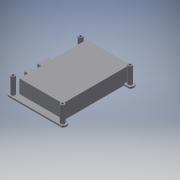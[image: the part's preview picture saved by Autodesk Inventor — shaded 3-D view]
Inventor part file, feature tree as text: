
AUTODESK INVENTOR PART (.ipt)
format: ipt  version: 2019 (Build 230136000, 136)  size: 1,348,608 bytes
history: native  units: mm
features: sketch x7, extrude x5, other x1
ambient origin geometry x8: Origin, YZ Plane, XZ Plane, XY Plane, X Axis, Y Axis, Z Axis, Center Point
bodies: Solid1 (feature_tree)
feature tree (13):
  extrude  "Extrusion1"  Depth=98.58mm
  extrude  "Extrusion2"  Depth=90.0mm
  extrude  "Extrusion3"  Depth=3.0mm
  extrude  "Extrusion4"  Depth=3.0mm
  sketch  "Sketch6"  dims[d8=76.54mm d9=98.58mm]
  extrude  "Extrusion5"  Depth=98.58mm
  sketch  "Sketch8"  dims[d11=81.43mm d12=7.0mm d13=7.0mm d14=2.0mm d15=0.0mm d16=58.04mm d17=98.58mm d18=90.0mm d19=18.0mm d20=0.0mm d21=46.0mm d22=15.0mm d23=20.0mm d24=15.0mm d25=20.0mm d26=8.0mm d27=8.0mm d28=20.0mm d29=5.0mm d30=0.0mm d31=3.0mm d32=3.0mm d33=3.0mm d34=3.0mm d35=5.0mm d36=5.0mm d37=5.0mm d38=5.0mm d39=22.0mm d40=0.0mm d41=27.0mm d42=52.0mm d43=16.0mm d44=2.0mm d45=0.0mm]
  sketch  "Sketch1"  dims[d0=58.04mm d1=98.58mm]
  sketch  "Sketch2"  dims[d2=66.0mm d3=90.0mm]
  sketch  "Sketch3"  dims[d4=3.0mm d5=3.0mm]
  sketch  "Sketch5"  dims[d6=3.0mm d7=3.0mm]
  sketch  "Sketch7"  dims[d10=76.54mm]
  other  "Image1"
